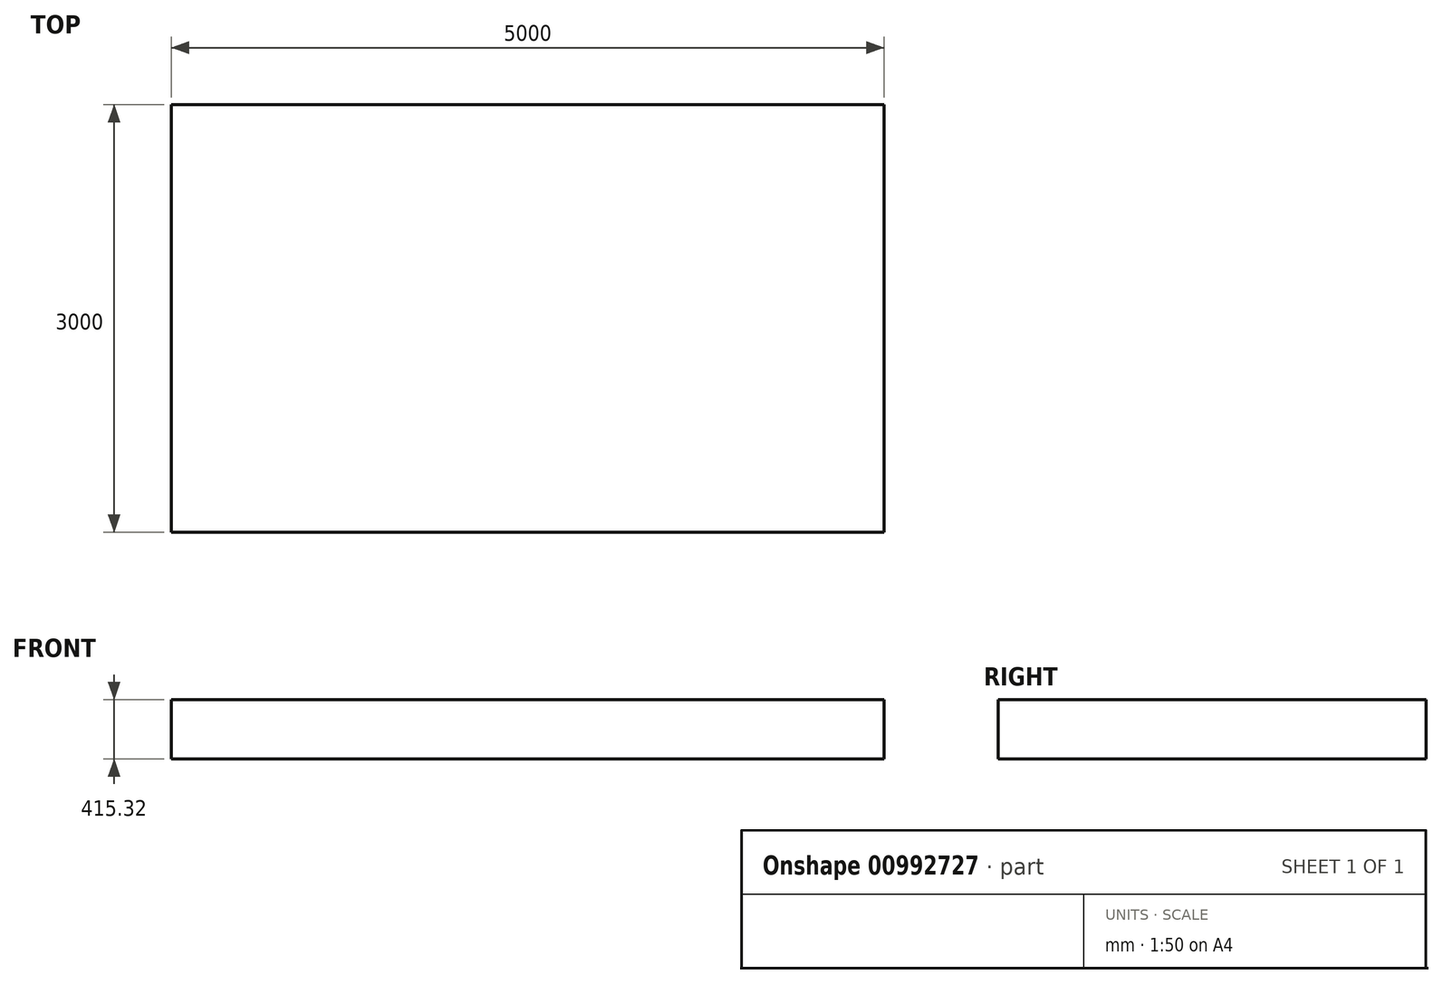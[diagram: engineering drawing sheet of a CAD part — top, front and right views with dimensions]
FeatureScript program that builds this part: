
annotation { "Feature Type Name" : "Feature", "Feature Type Description" : "" }
export const myFeature = defineFeature(function(context is Context, id is Id, definition is map)
    precondition{}
    {
        {
            var Q0;
            Q0=qCreatedBy(makeId("Front.planeOp"),FACE);
            var sketch = newSketch(context, id + "F0", { "sketchPlane" : qUnion([Q0])});
            skLineSegment(sketch, "E0.bottom", {"start": v(-2500, 207.66) * mm, "end": v(2500, 207.66) * mm});
            skLineSegment(sketch, "E0.top", {"start": v(-2500, -207.66) * mm, "end": v(2500, -207.66) * mm});
            skLineSegment(sketch, "E0.left", {"start": v(-2500, 207.66) * mm, "end": v(-2500, -207.66) * mm});
            skLineSegment(sketch, "E0.right", {"start": v(2500, 207.66) * mm, "end": v(2500, -207.66) * mm});
            skPoint(sketch, "E0.middle", {"position": v(0, 0) * mm});
            skSolve(sketch);
        }
        {
            var Q0;
            Q0=makeQuery(id+"F0.imprint","IMPRINT",FACE,{"disambiguationData":[TD([[makeQuery(id+"F0.imprint","IMPRINT",EDGE,{"derivedFrom":sQuery(id+"F0.wireOp",EDGE,"E0.bottom")}),-1.0]])]});
            extrude(context, id + "F1", {"entities" : qUnion([Q0]), "depth" : 3000 * mm, "offsetDistance" : 25 * mm});
        }
        {
            var Q0;
            Q0=makeQuery(id+"F1.opExtrude","SWEPT_FACE",FACE,{"disambiguationData":[OSD([sQuery(id+"F0.wireOp",EDGE,"E0.bottom")])]});
            var sketch = newSketch(context, id + "F2", { "sketchPlane" : qUnion([Q0])});
            skLineSegment(sketch, "E1", {"start": v(-2500, -1500) * mm, "end": v(2500, -1500) * mm});
            skSolve(sketch);
        }
        {
            var Q0;
            {var subQ0=sQuery(id+"F2.wireOp",EDGE,"E1");Q0=makeQuery(id+"F2.imprint","IMPRINT",FACE,{"disambiguationData":[TD([[makeQuery(id+"F2.imprint","IMPRINT",EDGE,{"derivedFrom":subQ0}),-1.0]])]});}
            var sketch = newSketch(context, id + "F3", { "sketchPlane" : qUnion([Q0])});
            skPoint(sketch, "E2", {"position": v(-2500.01, -1499.86) * mm});
            skLineSegment(sketch, "E3", {"start": v(-2500.01, -1499.86) * mm, "end": v(-2500.01, -1603.88) * mm});
            skLineSegment(sketch, "E4", {"start": v(-2500.01, -1603.88) * mm, "end": v(-2500.01, -1403.88) * mm});
            skLineSegment(sketch, "E5", {"start": v(-2500.01, -1603.88) * mm, "end": v(-2400.01, -1603.88) * mm});
            skLineSegment(sketch, "E6", {"start": v(-2400.01, -1603.88) * mm, "end": v(-2400.01, -1403.88) * mm});
            skLineSegment(sketch, "E7", {"start": v(-2400.01, -1403.88) * mm, "end": v(-2500.01, -1403.88) * mm});
            skSolve(sketch);
        }
        {
            var Q0;
            Q0=sQuery(id+"F3.wireOp",EDGE,"E7");
            var Q1;
            Q1=sQuery(id+"F3.wireOp",EDGE,"E6");
            var Q2;
            Q2=sQuery(id+"F3.wireOp",EDGE,"E4");
            var Q3;
            Q3=sQuery(id+"F3.wireOp",EDGE,"E5");
            extrude(context, id + "F4", {"bodyType" : ToolBodyType.SURFACE, "surfaceEntities" : qUnion([Q0, Q1, Q2, Q3]), "endBound" : BoundingType.THROUGH_ALL, "depth" : 25 * mm, "offsetDistance" : 25 * mm});
        }
    });
